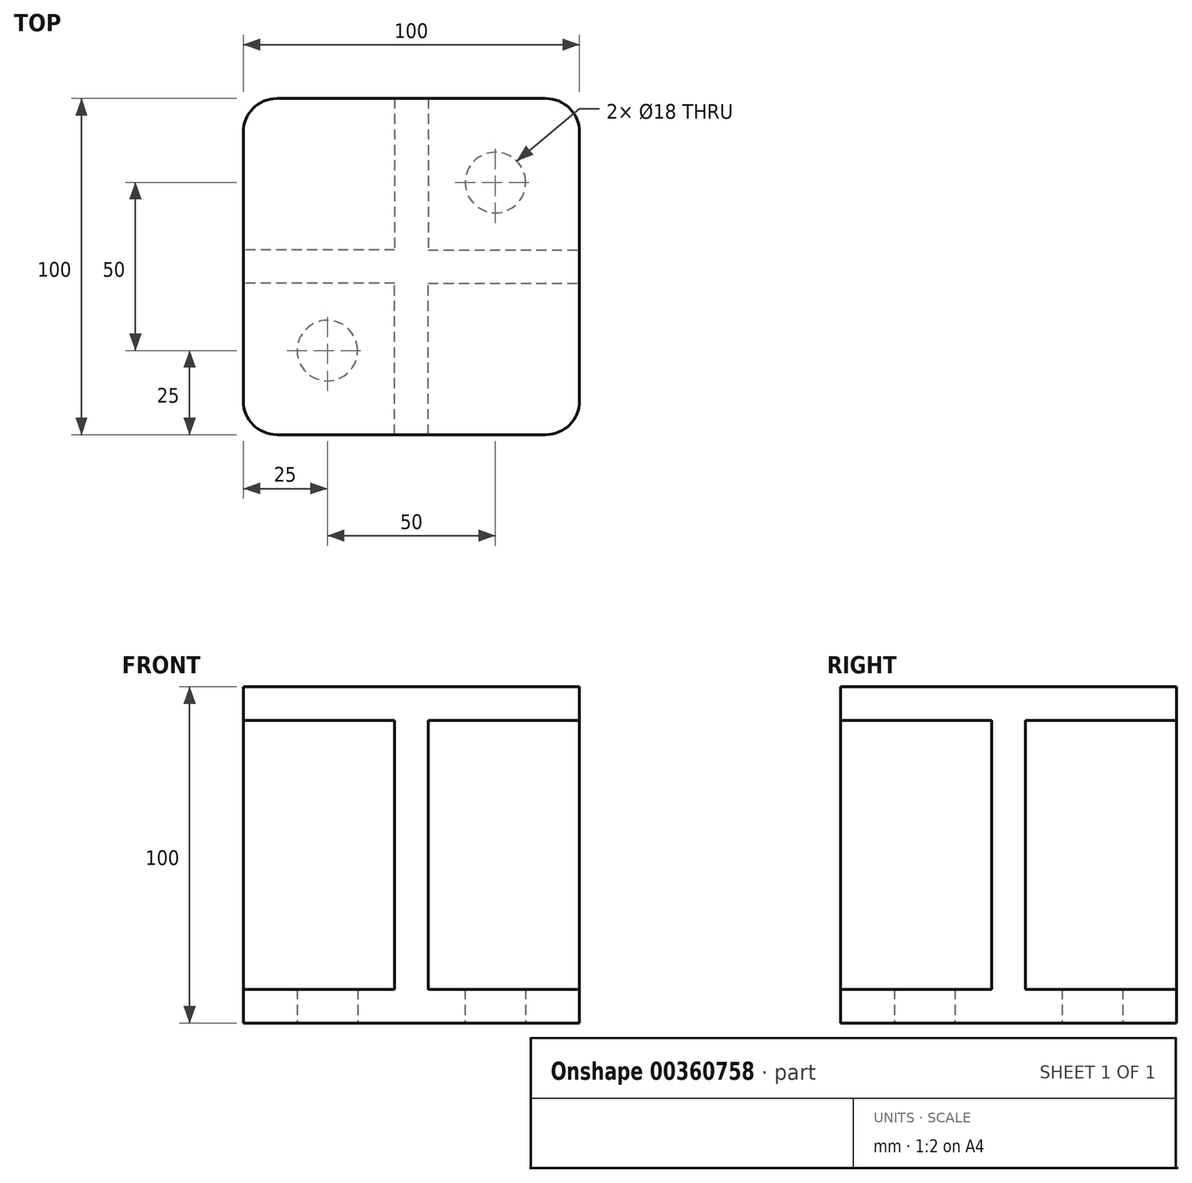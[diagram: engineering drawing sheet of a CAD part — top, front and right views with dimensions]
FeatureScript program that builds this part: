
annotation { "Feature Type Name" : "Feature", "Feature Type Description" : "" }
export const myFeature = defineFeature(function(context is Context, id is Id, definition is map)
    precondition{}
    {
        {
            var Q0;
            Q0=qCreatedBy(makeId("Top.planeOp"),FACE);
            var sketch = newSketch(context, id + "F0", { "sketchPlane" : qUnion([Q0])});
            skLineSegment(sketch, "E0", {"start": v(0, -50) * mm, "end": v(5, -50) * mm});
            skLineSegment(sketch, "E1", {"start": v(5, -50) * mm, "end": v(5, -5) * mm});
            skLineSegment(sketch, "E2", {"start": v(5, -5) * mm, "end": v(50, -5) * mm});
            skLineSegment(sketch, "E3", {"start": v(50, -5) * mm, "end": v(50, 0) * mm});
            skLineSegment(sketch, "E4.MirrorCS", {"start": v(50, 5) * mm, "end": v(50, 0) * mm});
            skLineSegment(sketch, "E5.MirrorCS", {"start": v(5, 5) * mm, "end": v(50, 5) * mm});
            skLineSegment(sketch, "E6.MirrorCS", {"start": v(5, 50) * mm, "end": v(5, 5) * mm});
            skLineSegment(sketch, "E7.MirrorCS", {"start": v(0, 50) * mm, "end": v(5, 50) * mm});
            skLineSegment(sketch, "E8.MirrorCS", {"start": v(0, 50) * mm, "end": v(-5, 50) * mm});
            skLineSegment(sketch, "E9.MirrorCS", {"start": v(-5, 50) * mm, "end": v(-5, 5) * mm});
            skLineSegment(sketch, "E10.MirrorCS", {"start": v(-5, 5) * mm, "end": v(-50, 5) * mm});
            skLineSegment(sketch, "E11.MirrorCS", {"start": v(-50, 5) * mm, "end": v(-50, 0) * mm});
            skLineSegment(sketch, "E12.MirrorCS", {"start": v(-50, -5) * mm, "end": v(-50, 0) * mm});
            skLineSegment(sketch, "E13.MirrorCS", {"start": v(-5, -5) * mm, "end": v(-50, -5) * mm});
            skLineSegment(sketch, "E14.MirrorCS", {"start": v(-5, -50) * mm, "end": v(-5, -5) * mm});
            skLineSegment(sketch, "E15.MirrorCS", {"start": v(0, -50) * mm, "end": v(-5, -50) * mm});
            skSolve(sketch);
        }
        {
            var Q0;
            Q0=makeQuery(id+"F0.imprint","IMPRINT",FACE,{"disambiguationData":[TD([[makeQuery(id+"F0.imprint","IMPRINT",EDGE,{"derivedFrom":sQuery(id+"F0.wireOp",EDGE,"E0")}),1.0]])]});
            extrude(context, id + "F1", {"entities" : qUnion([Q0]), "depth" : 100 * mm});
        }
        {
            var Q0;
            Q0=qCreatedBy(makeId("Top.planeOp"),FACE);
            var sketch = newSketch(context, id + "F2", { "sketchPlane" : qUnion([Q0])});
            skLineSegment(sketch, "E16.bottom", {"start": v(-50, -50) * mm, "end": v(50, -50) * mm});
            skLineSegment(sketch, "E16.top", {"start": v(-50, 50) * mm, "end": v(50, 50) * mm});
            skLineSegment(sketch, "E16.left", {"start": v(-50, -50) * mm, "end": v(-50, 50) * mm});
            skLineSegment(sketch, "E16.right", {"start": v(50, -50) * mm, "end": v(50, 50) * mm});
            skSolve(sketch);
        }
        {
            var Q0;
            Q0=makeQuery(id+"F2.imprint","IMPRINT",FACE,{"disambiguationData":[TD([[makeQuery(id+"F2.imprint","IMPRINT",EDGE,{"derivedFrom":sQuery(id+"F2.wireOp",EDGE,"E16.bottom")}),1.0]])]});
            extrude(context, id + "F3", {"entities" : qUnion([Q0]), "operationType" : NewBodyOperationType.ADD, "depth" : 10 * mm});
        }
        {
            var Q0;
            Q0=makeQuery(id+"F1.opExtrude","CAP_FACE",FACE,{"disambiguationData":[OSD([sQuery(id+"F0.wireOp",EDGE,"E0"),sQuery(id+"F0.wireOp",EDGE,"E1"),sQuery(id+"F0.wireOp",EDGE,"E2"),sQuery(id+"F0.wireOp",EDGE,"E3"),sQuery(id+"F0.wireOp",EDGE,"E4.MirrorCS"),sQuery(id+"F0.wireOp",EDGE,"E5.MirrorCS"),sQuery(id+"F0.wireOp",EDGE,"E6.MirrorCS"),sQuery(id+"F0.wireOp",EDGE,"E7.MirrorCS"),sQuery(id+"F0.wireOp",EDGE,"E8.MirrorCS"),sQuery(id+"F0.wireOp",EDGE,"E9.MirrorCS"),sQuery(id+"F0.wireOp",EDGE,"E10.MirrorCS"),sQuery(id+"F0.wireOp",EDGE,"E11.MirrorCS"),sQuery(id+"F0.wireOp",EDGE,"E12.MirrorCS"),sQuery(id+"F0.wireOp",EDGE,"E13.MirrorCS"),sQuery(id+"F0.wireOp",EDGE,"E14.MirrorCS"),sQuery(id+"F0.wireOp",EDGE,"E15.MirrorCS")])],"isStart":false});
            var sketch = newSketch(context, id + "F4", { "sketchPlane" : qUnion([Q0])});
            skLineSegment(sketch, "E17.bottom", {"start": v(-50, 50) * mm, "end": v(50, 50) * mm});
            skLineSegment(sketch, "E17.top", {"start": v(-50, -50) * mm, "end": v(50, -50) * mm});
            skLineSegment(sketch, "E17.left", {"start": v(-50, 50) * mm, "end": v(-50, -50) * mm});
            skLineSegment(sketch, "E17.right", {"start": v(50, 50) * mm, "end": v(50, -50) * mm});
            skSolve(sketch);
        }
        {
            var Q0;
            {var subQ1=makeQuery(id+"F1.opExtrude","CAP_EDGE",EDGE,{"disambiguationData":[OSD([sQuery(id+"F0.wireOp",EDGE,"E9.MirrorCS")])],"isStart":false});Q0=makeQuery(id+"F4.imprint","IMPRINT",FACE,{"disambiguationData":[TD([[makeQuery(id+"F4.imprint","IMPRINT",EDGE,{"derivedFrom":subQ1}),-1.0]])]});}
            var Q1;
            {var subQ4=makeQuery(id+"F1.opExtrude","CAP_EDGE",EDGE,{"disambiguationData":[OSD([sQuery(id+"F0.wireOp",EDGE,"E1")])],"isStart":false});Q1=makeQuery(id+"F4.imprint","IMPRINT",FACE,{"disambiguationData":[TD([[makeQuery(id+"F4.imprint","IMPRINT",EDGE,{"derivedFrom":subQ4}),1.0]])]});}
            var Q2;
            {var subQ4=makeQuery(id+"F1.opExtrude","CAP_EDGE",EDGE,{"disambiguationData":[OSD([sQuery(id+"F0.wireOp",EDGE,"E5.MirrorCS")])],"isStart":false});Q2=makeQuery(id+"F4.imprint","IMPRINT",FACE,{"disambiguationData":[TD([[makeQuery(id+"F4.imprint","IMPRINT",EDGE,{"derivedFrom":subQ4}),1.0]])]});}
            var Q3;
            {var subQ1=makeQuery(id+"F1.opExtrude","CAP_EDGE",EDGE,{"disambiguationData":[OSD([sQuery(id+"F0.wireOp",EDGE,"E1")])],"isStart":false});Q3=makeQuery(id+"F4.imprint","IMPRINT",FACE,{"disambiguationData":[TD([[makeQuery(id+"F4.imprint","IMPRINT",EDGE,{"derivedFrom":subQ1}),-1.0]])]});}
            var Q4;
            {var subQ4=makeQuery(id+"F1.opExtrude","CAP_EDGE",EDGE,{"disambiguationData":[OSD([sQuery(id+"F0.wireOp",EDGE,"E13.MirrorCS")])],"isStart":false});Q4=makeQuery(id+"F4.imprint","IMPRINT",FACE,{"disambiguationData":[TD([[makeQuery(id+"F4.imprint","IMPRINT",EDGE,{"derivedFrom":subQ4}),1.0]])]});}
            extrude(context, id + "F5", {"entities" : qUnion([Q0, Q1, Q2, Q3, Q4]), "operationType" : NewBodyOperationType.ADD, "oppositeDirection" : true, "depth" : 10 * mm});
        }
        {
            var Q0;
            Q0=makeQuery(id+"F5.opExtrude","SWEPT_EDGE",EDGE,{"disambiguationData":[OSD([sQuery(id+"F4.wireOp",EDGE,"E17.top"),sQuery(id+"F4.wireOp",EDGE,"E17.right")])]});
            var Q1;
            Q1=makeQuery(id+"F3.opExtrude","SWEPT_EDGE",EDGE,{"disambiguationData":[OSD([sQuery(id+"F2.wireOp",EDGE,"E16.bottom"),sQuery(id+"F2.wireOp",EDGE,"E16.right")])]});
            var Q2;
            Q2=makeQuery(id+"F5.opExtrude","SWEPT_EDGE",EDGE,{"disambiguationData":[OSD([sQuery(id+"F4.wireOp",EDGE,"E17.bottom"),sQuery(id+"F4.wireOp",EDGE,"E17.right")])]});
            var Q3;
            Q3=makeQuery(id+"F3.opExtrude","SWEPT_EDGE",EDGE,{"disambiguationData":[OSD([sQuery(id+"F2.wireOp",EDGE,"E16.top"),sQuery(id+"F2.wireOp",EDGE,"E16.right")])]});
            var Q4;
            Q4=makeQuery(id+"F5.opExtrude","SWEPT_EDGE",EDGE,{"disambiguationData":[OSD([sQuery(id+"F4.wireOp",EDGE,"E17.top"),sQuery(id+"F4.wireOp",EDGE,"E17.left")])]});
            var Q5;
            Q5=makeQuery(id+"F3.opExtrude","SWEPT_EDGE",EDGE,{"disambiguationData":[OSD([sQuery(id+"F2.wireOp",EDGE,"E16.bottom"),sQuery(id+"F2.wireOp",EDGE,"E16.left")])]});
            var Q6;
            Q6=makeQuery(id+"F5.opExtrude","SWEPT_EDGE",EDGE,{"disambiguationData":[OSD([sQuery(id+"F4.wireOp",EDGE,"E17.bottom"),sQuery(id+"F4.wireOp",EDGE,"E17.left")])]});
            var Q7;
            Q7=makeQuery(id+"F3.opExtrude","SWEPT_EDGE",EDGE,{"disambiguationData":[OSD([sQuery(id+"F2.wireOp",EDGE,"E16.top"),sQuery(id+"F2.wireOp",EDGE,"E16.left")])]});
            fillet(context, id + "F6", {"entities" : qUnion([Q0, Q1, Q2, Q3, Q4, Q5, Q6, Q7]), "radius" : 10 * mm, "tangentPropagation" : true, "allowEdgeOverflow" : false});
        }
        {
            var Q0;
            Q0=qCreatedBy(makeId("Top.planeOp"),FACE);
            var sketch = newSketch(context, id + "F7", { "sketchPlane" : qUnion([Q0])});
            skCircle(sketch, "E18.0.1.0", {"center": v(-25, -25) * mm, "radius": 9 * mm});
            skCircle(sketch, "E18.1.0.0", {"center": v(25, 25) * mm, "radius": 9 * mm});
            skLineSegment(sketch, "E18.direction1", {"start": v(-25, 25) * mm, "end": v(25, 25) * mm, "construction": true});
            skLineSegment(sketch, "E18.direction2", {"start": v(-25, 25) * mm, "end": v(-25, -25) * mm, "construction": true});
            skSolve(sketch);
        }
        {
            var Q0;
            Q0=qSketchRegion(id+"F7",true);
            extrude(context, id + "F8", {"entities" : qUnion([Q0]), "operationType" : NewBodyOperationType.REMOVE, "endBound" : BoundingType.SYMMETRIC, "depth" : 174 * mm});
        }
    });
